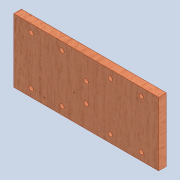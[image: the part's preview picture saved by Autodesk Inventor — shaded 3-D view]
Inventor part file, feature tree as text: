
AUTODESK INVENTOR PART (.ipt)
format: ipt  version: 2020 (Build 240168000, 168)  size: 160,768 bytes
history: native  units: mm
features: extrude x2, sketch x2
ambient origin geometry x8: Origin, YZ Plane, XZ Plane, XY Plane, X Axis, Y Axis, Z Axis, Center Point
bodies: Solid1 (feature_tree)
feature tree (4):
  extrude  "Extrusion1"  Depth=66.0mm
  extrude  "Extrusion4"  Depth=10.0mm
  sketch  "Sketch1"  dims[d0=150.0mm d1=66.0mm]
  sketch  "Sketch4"  dims[d2=8.0mm d3=0.0mm d19=4.5mm d20=18.0mm d21=8.0mm d22=8.0mm d23=32.0mm d24=18.0mm d26=32.0mm d27=0.0mm d28=0.0mm d29=10.0mm d30=10.0mm]
